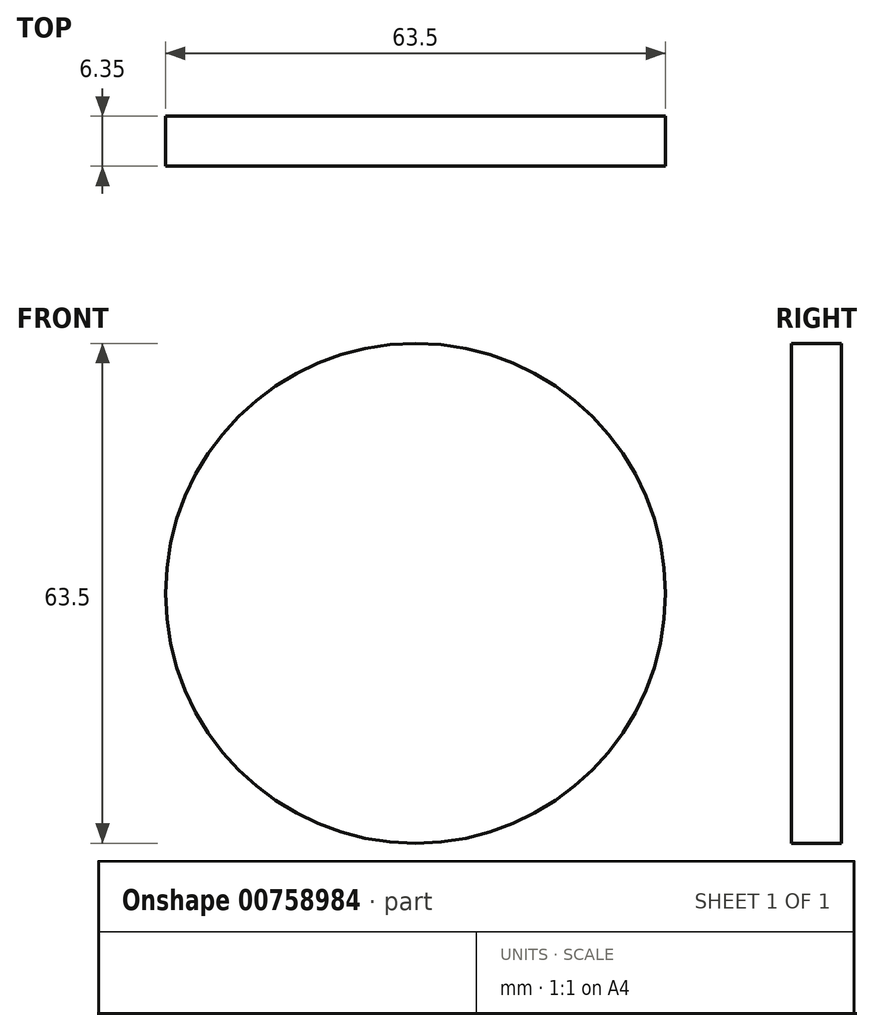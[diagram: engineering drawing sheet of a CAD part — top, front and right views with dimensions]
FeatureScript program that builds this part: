
annotation { "Feature Type Name" : "Feature", "Feature Type Description" : "" }
export const myFeature = defineFeature(function(context is Context, id is Id, definition is map)
    precondition{}
    {
        {
            var Q0;
            Q0=qCreatedBy(makeId("Front.planeOp"),FACE);
            var sketch = newSketch(context, id + "F0", { "sketchPlane" : qUnion([Q0])});
            skCircle(sketch, "E0", {"center": v(0, 0) * mm, "radius": 31.75 * mm});
            skSolve(sketch);
        }
        {
            var Q0;
            Q0 = qSketchRegion(id + "F0", true);
            extrude(context, id + "F1", {"entities" : qUnion([Q0]), "depth" : 6.35 * mm, "offsetDistance" : 25.4 * mm});
        }
    });
